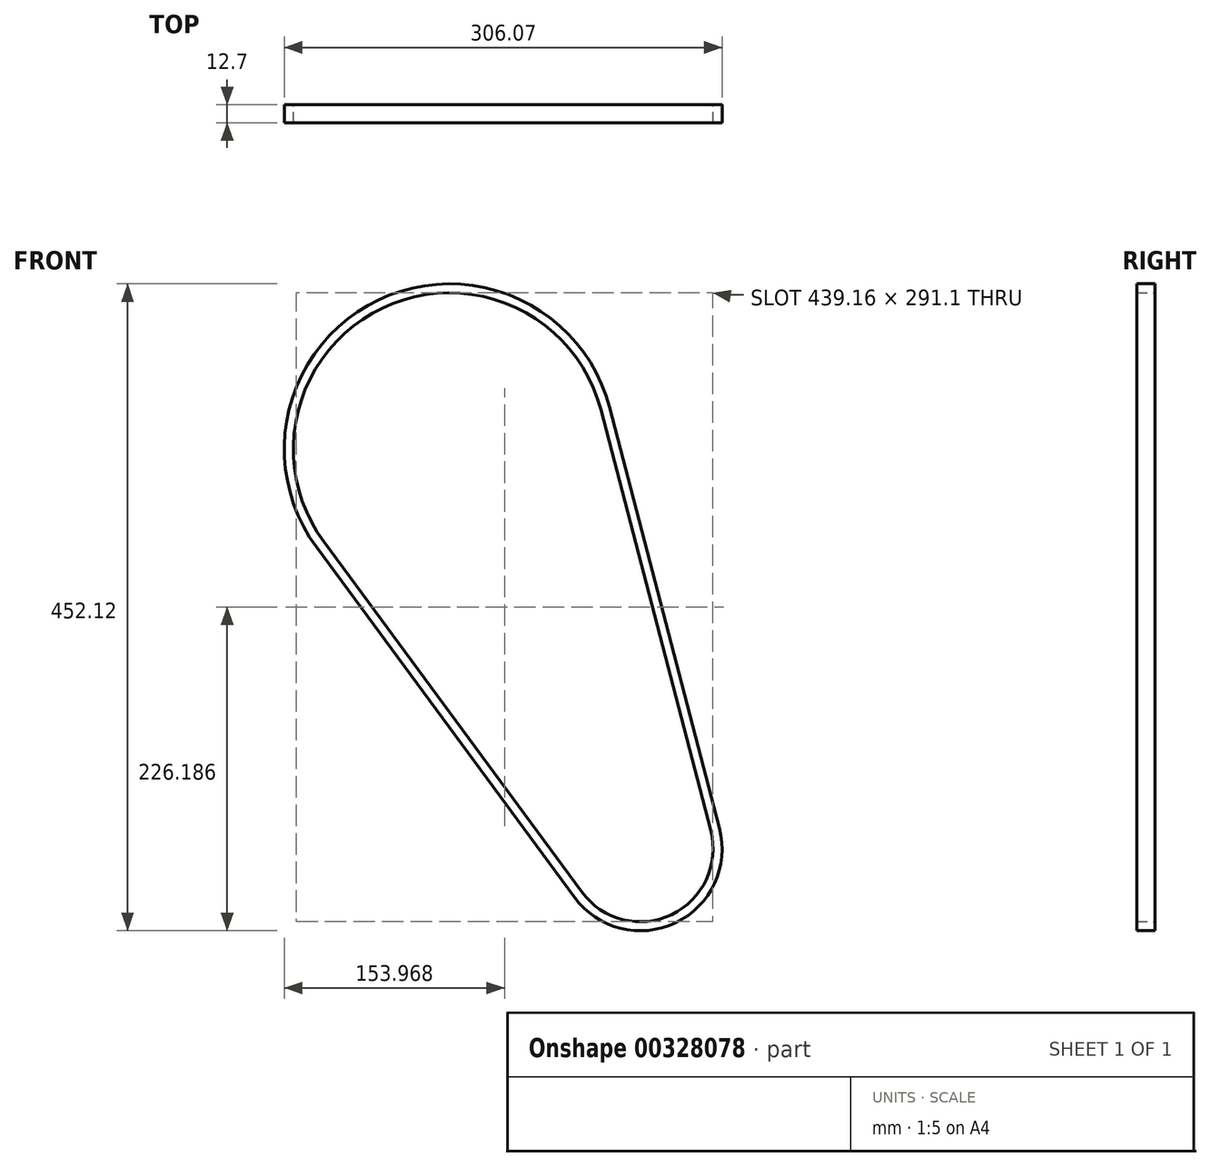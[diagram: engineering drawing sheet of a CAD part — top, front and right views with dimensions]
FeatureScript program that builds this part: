
annotation { "Feature Type Name" : "Feature", "Feature Type Description" : "" }
export const myFeature = defineFeature(function(context is Context, id is Id, definition is map)
    precondition{}
    {
        {
            var Q0;
            Q0=qCreatedBy(makeId("Front.planeOp"),FACE);
            var sketch = newSketch(context, id + "F0", { "sketchPlane" : qUnion([Q0])});
            skLineSegment(sketch, "E0", {"start": v(0, 0) * mm, "end": v(0, -279.4) * mm, "construction": true});
            skLineSegment(sketch, "E1", {"start": v(0, -279.4) * mm, "end": v(133.35, -279.4) * mm, "construction": true});
            skArc(sketch, "E2", {"start": v(105.68, 27.6) * mm, "mid": v(-47.04, 98.57) * mm, "end": v(-87.92, -64.8) * mm});
            skArc(sketch, "E3", {"start": v(92.46, -309.54) * mm, "mid": v(155.23, -325.25) * mm, "end": v(182.5, -266.56) * mm});
            skLineSegment(sketch, "E4", {"start": v(0, 0) * mm, "end": v(133.35, -279.4) * mm, "construction": true});
            skLineSegment(sketch, "E5", {"start": v(103.12, 37.4) * mm, "end": v(182.5, -266.56) * mm});
            skLineSegment(sketch, "E6.MirrorCS", {"start": v(-93.92, -56.65) * mm, "end": v(92.46, -309.54) * mm});
            skArc(sketch, "E7.0", {"start": v(111.82, 29.2) * mm, "mid": v(-49.78, 104.3) * mm, "end": v(-93.03, -68.57) * mm});
            skLineSegment(sketch, "E8.0", {"start": v(109.26, 39) * mm, "end": v(188.65, -264.96) * mm});
            skArc(sketch, "E9.0", {"start": v(87.34, -313.3) * mm, "mid": v(157.97, -330.98) * mm, "end": v(188.65, -264.96) * mm});
            skLineSegment(sketch, "E10.0", {"start": v(-99.04, -60.42) * mm, "end": v(87.34, -313.3) * mm});
            skSolve(sketch);
        }
        {
            var Q0;
            Q0 = qSketchRegion(id + "F0", true);
            extrude(context, id + "F1", {"entities" : qUnion([Q0]), "endBound" : BoundingType.SYMMETRIC, "depth" : 12.7 * mm});
        }
    });
